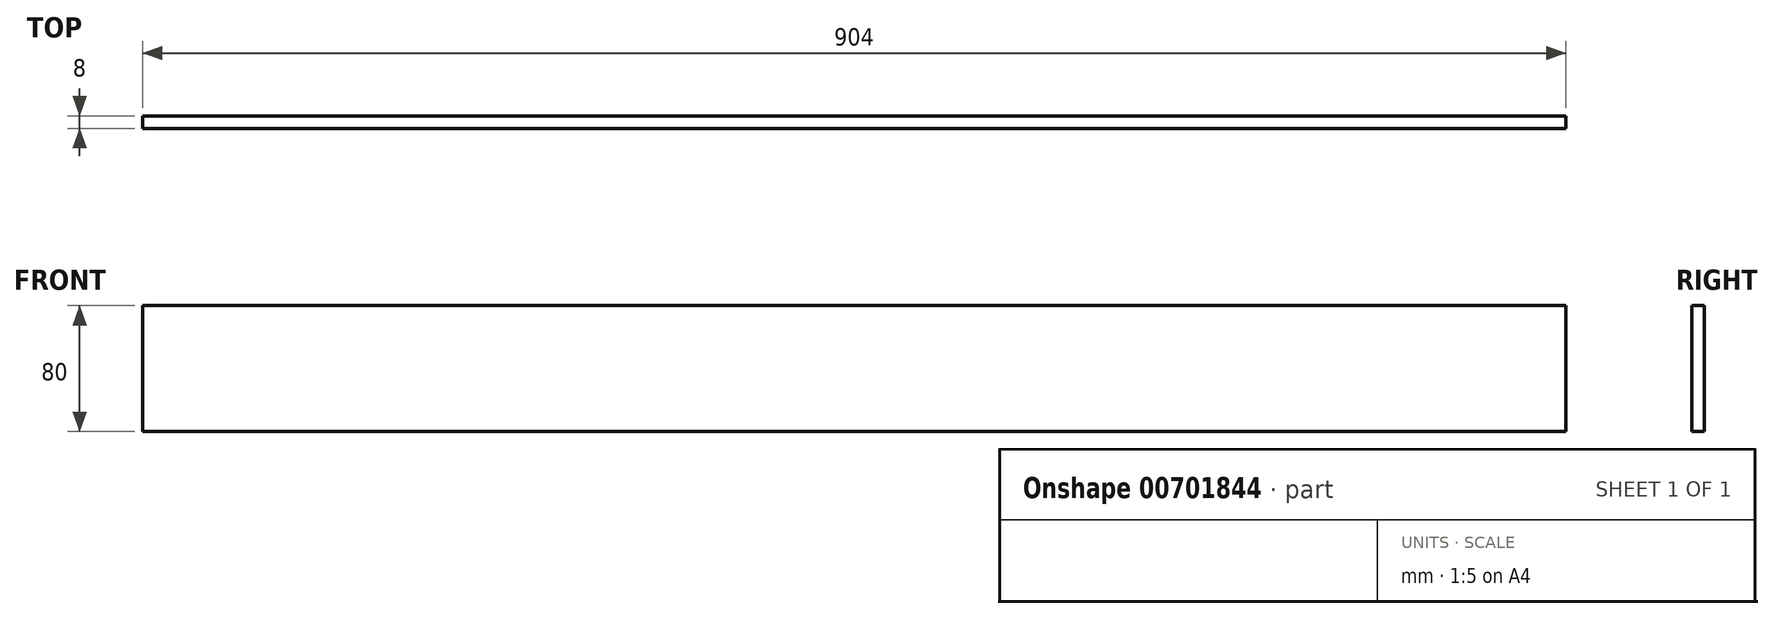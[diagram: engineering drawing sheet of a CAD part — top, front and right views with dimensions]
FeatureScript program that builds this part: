
annotation { "Feature Type Name" : "Feature", "Feature Type Description" : "" }
export const myFeature = defineFeature(function(context is Context, id is Id, definition is map)
    precondition{}
    {
        {
            var Q0;
            Q0=qCreatedBy(makeId("Front.planeOp"),FACE);
            var sketch = newSketch(context, id + "F0", { "sketchPlane" : qUnion([Q0])});
            skLineSegment(sketch, "E0.bottom", {"start": v(0, 0) * mm, "end": v(904, 0) * mm});
            skLineSegment(sketch, "E0.top", {"start": v(0, 80) * mm, "end": v(904, 80) * mm});
            skLineSegment(sketch, "E0.left", {"start": v(0, 0) * mm, "end": v(0, 80) * mm});
            skLineSegment(sketch, "E0.right", {"start": v(904, 0) * mm, "end": v(904, 80) * mm});
            skSolve(sketch);
        }
        {
            var Q0;
            Q0 = qSketchRegion(id + "F0", true);
            extrude(context, id + "F1", {"entities" : qUnion([Q0]), "depth" : 8 * mm, "offsetDistance" : 25 * mm});
        }
    });
